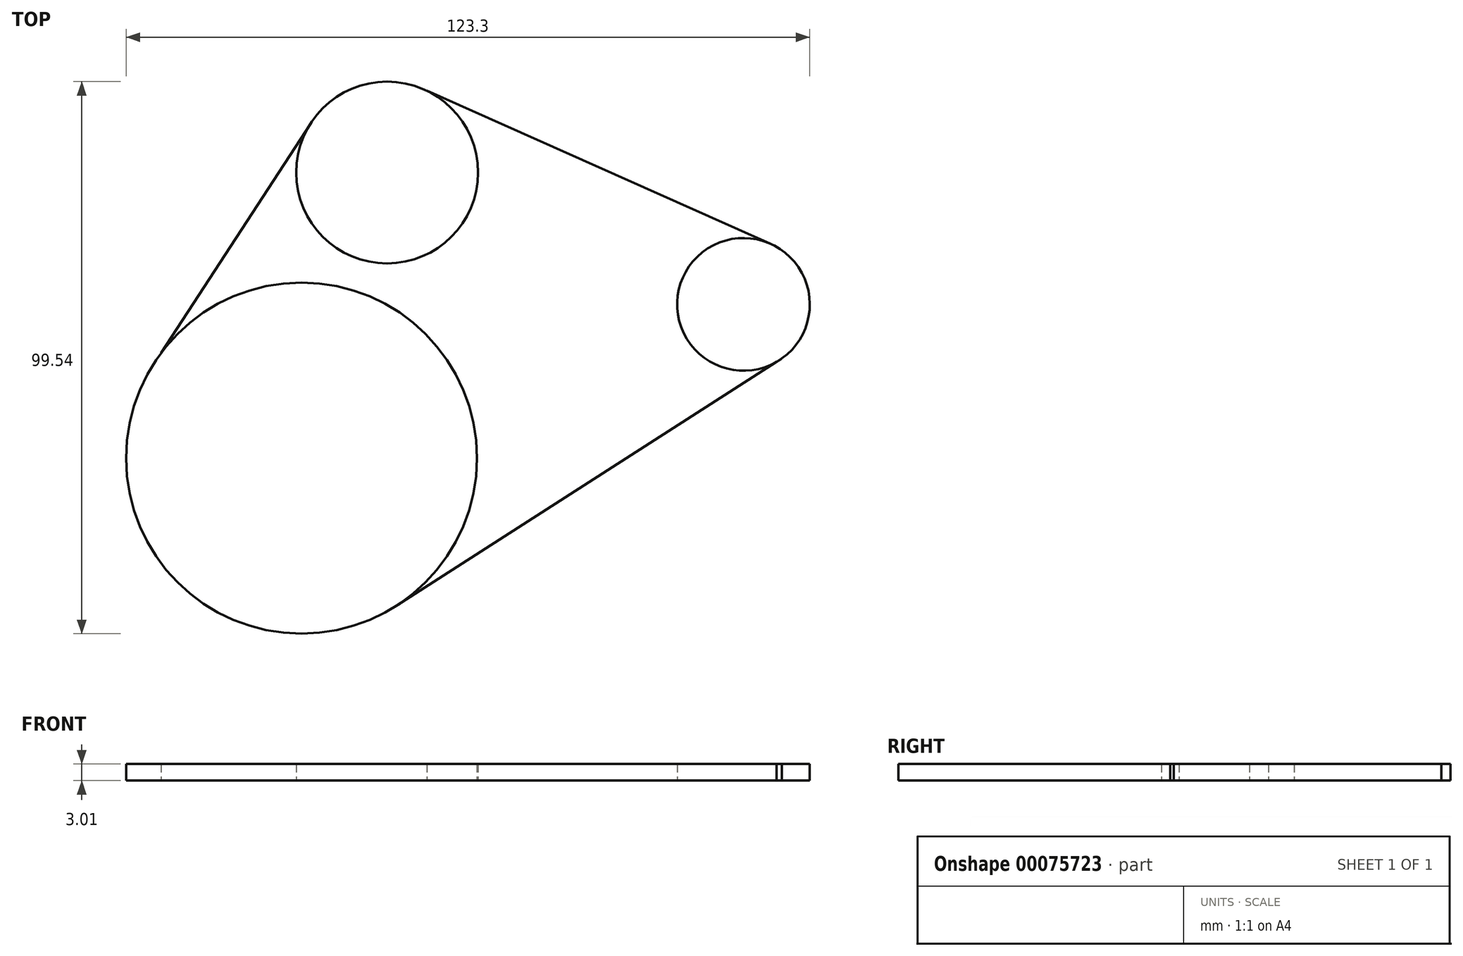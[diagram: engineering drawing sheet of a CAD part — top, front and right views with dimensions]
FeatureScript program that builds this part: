
annotation { "Feature Type Name" : "Feature", "Feature Type Description" : "" }
export const myFeature = defineFeature(function(context is Context, id is Id, definition is map)
    precondition{}
    {
        {
            var Q0;
            Q0=qCreatedBy(makeId("Top.planeOp"),FACE);
            var sketch = newSketch(context, id + "F0", { "sketchPlane" : qUnion([Q0])});
            skCircle(sketch, "E0", {"center": v(-37.54, 31.1) * mm, "radius": 16.4 * mm});
            skCircle(sketch, "E1", {"center": v(26.73, 7.33) * mm, "radius": 11.96 * mm});
            skCircle(sketch, "E2", {"center": v(-52.97, -20.4) * mm, "radius": 31.64 * mm});
            skLineSegment(sketch, "E3", {"start": v(-78.3, -1.42) * mm, "end": v(-51.28, 40.05) * mm});
            skLineSegment(sketch, "E4", {"start": v(-30.37, 45.85) * mm, "end": v(31.6, 18.25) * mm});
            skLineSegment(sketch, "E5", {"start": v(33.67, -2.42) * mm, "end": v(-35.88, -47.03) * mm});
            skSolve(sketch);
        }
        {
            var Q0;
            Q0 = qSketchRegion(id + "F0", true);
            extrude(context, id + "F1", {"entities" : qUnion([Q0]), "depth" : 3 * mm});
        }
        {
            var Q0;
            {var subQ0=sQuery(id+"F0.wireOp",EDGE,"E2");var subQ1=makeQuery(id+"F0.imprint","INTERSECT",VERTEX,{"derivedFrom":[subQ0,sQuery(id+"F0.wireOp",EDGE,"E3")]});Q0=makeQuery(id+"F0.imprint","IMPRINT",FACE,{"disambiguationData":[TD([[makeQuery(id+"F0.imprint","IMPRINT",EDGE,{"disambiguationData":[TD([[subQ1,-1.0]])],"derivedFrom":subQ0}),1.0]])]});}
            var Q1;
            {var subQ0=sQuery(id+"F0.wireOp",EDGE,"E1");var subQ1=makeQuery(id+"F0.imprint","INTERSECT",VERTEX,{"derivedFrom":[subQ0,sQuery(id+"F0.wireOp",EDGE,"E4")]});Q1=makeQuery(id+"F0.imprint","IMPRINT",FACE,{"disambiguationData":[TD([[makeQuery(id+"F0.imprint","IMPRINT",EDGE,{"disambiguationData":[TD([[subQ1,-1.0]])],"derivedFrom":subQ0}),1.0]])]});}
            var Q2;
            {var subQ0=sQuery(id+"F0.wireOp",EDGE,"E0");var subQ1=makeQuery(id+"F0.imprint","INTERSECT",VERTEX,{"derivedFrom":[subQ0,sQuery(id+"F0.wireOp",EDGE,"E3")]});Q2=makeQuery(id+"F0.imprint","IMPRINT",FACE,{"disambiguationData":[TD([[makeQuery(id+"F0.imprint","IMPRINT",EDGE,{"disambiguationData":[TD([[subQ1,1.0]])],"derivedFrom":subQ0}),1.0]])]});}
            extrude(context, id + "F2", {"entities" : qUnion([Q0, Q1, Q2]), "depth" : 3 * mm});
        }
    });
